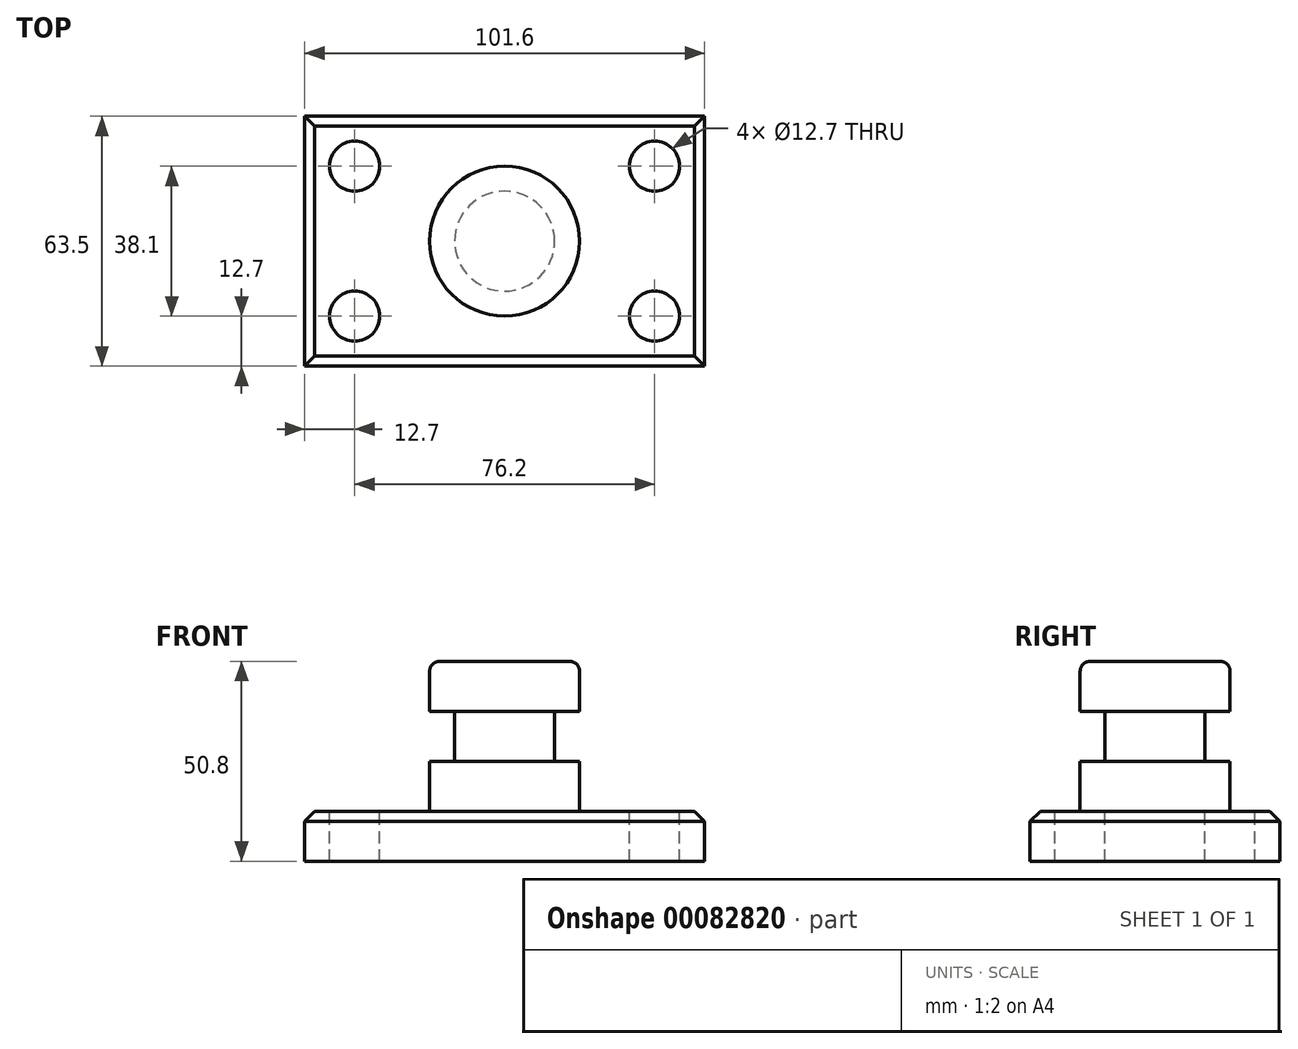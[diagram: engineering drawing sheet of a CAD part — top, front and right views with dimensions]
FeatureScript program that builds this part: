
annotation { "Feature Type Name" : "Feature", "Feature Type Description" : "" }
export const myFeature = defineFeature(function(context is Context, id is Id, definition is map)
    precondition{}
    {
        {
            var Q0;
            Q0=qCreatedBy(makeId("Top.planeOp"),FACE);
            var sketch = newSketch(context, id + "F0", { "sketchPlane" : qUnion([Q0])});
            skLineSegment(sketch, "E0.bottom", {"start": v(-50.8, 31.75) * mm, "end": v(50.8, 31.75) * mm});
            skLineSegment(sketch, "E0.top", {"start": v(-50.8, -31.75) * mm, "end": v(50.8, -31.75) * mm});
            skLineSegment(sketch, "E0.left", {"start": v(-50.8, 31.75) * mm, "end": v(-50.8, -31.75) * mm});
            skLineSegment(sketch, "E0.right", {"start": v(50.8, 31.75) * mm, "end": v(50.8, -31.75) * mm});
            skSolve(sketch);
        }
        {
            var Q0;
            Q0=makeQuery(id+"F0.imprint","IMPRINT",FACE,{"disambiguationData":[TD([[makeQuery(id+"F0.imprint","IMPRINT",EDGE,{"derivedFrom":sQuery(id+"F0.wireOp",EDGE,"E0.bottom")}),-1.0]])]});
            extrude(context, id + "F1", {"entities" : qUnion([Q0]), "depth" : 12.7 * mm});
        }
        {
            var Q0;
            Q0=makeQuery(id+"F1.opExtrude","CAP_FACE",FACE,{"disambiguationData":[OSD([sQuery(id+"F0.wireOp",EDGE,"E0.bottom"),sQuery(id+"F0.wireOp",EDGE,"E0.top"),sQuery(id+"F0.wireOp",EDGE,"E0.left"),sQuery(id+"F0.wireOp",EDGE,"E0.right")])],"isStart":false});
            var sketch = newSketch(context, id + "F2", { "sketchPlane" : qUnion([Q0])});
            skCircle(sketch, "E1", {"center": v(-38.1, 19.05) * mm, "radius": 6.35 * mm});
            skCircle(sketch, "E2", {"center": v(-38.1, -19.05) * mm, "radius": 6.35 * mm});
            skCircle(sketch, "E3.MirrorC", {"center": v(38.1, 19.05) * mm, "radius": 6.35 * mm});
            skCircle(sketch, "E4.MirrorC", {"center": v(38.1, -19.05) * mm, "radius": 6.35 * mm});
            skSolve(sketch);
        }
        {
            var Q0;
            Q0 = qSketchRegion(id + "F2", true);
            extrude(context, id + "F3", {"entities" : qUnion([Q0]), "operationType" : NewBodyOperationType.REMOVE, "endBound" : BoundingType.THROUGH_ALL, "oppositeDirection" : true, "depth" : 25.4 * mm});
        }
        {
            var Q0;
            Q0=qCreatedBy(makeId("Front.planeOp"),FACE);
            var sketch = newSketch(context, id + "F4", { "sketchPlane" : qUnion([Q0])});
            skLineSegment(sketch, "E5", {"start": v(0, 12.7) * mm, "end": v(0, 50.8) * mm});
            skLineSegment(sketch, "E6", {"start": v(0, 50.8) * mm, "end": v(-19.05, 50.8) * mm});
            skLineSegment(sketch, "E7", {"start": v(-19.05, 50.8) * mm, "end": v(-19.05, 12.7) * mm});
            skLineSegment(sketch, "E8", {"start": v(-19.05, 12.7) * mm, "end": v(0, 12.7) * mm});
            skSolve(sketch);
        }
        {
            var Q0;
            Q0 = qSketchRegion(id + "F4", true);
            var Q1;
            Q1=sQuery(id+"F4.wireOp",EDGE,"E5");
            revolve(context, id + "F5", {"operationType" : NewBodyOperationType.ADD, "entities" : qUnion([Q0]), "axis" : qUnion([Q1]), "revolveType" : RevolveType.FULL});
        }
        {
            var Q0;
            Q0=qCreatedBy(makeId("Front.planeOp"),FACE);
            var sketch = newSketch(context, id + "F6", { "sketchPlane" : qUnion([Q0])});
            skLineSegment(sketch, "E9.bottom", {"start": v(19.05, 38.1) * mm, "end": v(12.7, 38.1) * mm});
            skLineSegment(sketch, "E9.top", {"start": v(19.05, 25.4) * mm, "end": v(12.7, 25.4) * mm});
            skLineSegment(sketch, "E9.left", {"start": v(19.05, 38.1) * mm, "end": v(19.05, 25.4) * mm});
            skLineSegment(sketch, "E9.right", {"start": v(12.7, 38.1) * mm, "end": v(12.7, 25.4) * mm});
            skLineSegment(sketch, "E10", {"start": v(19.05, 50.8) * mm, "end": v(19.05, 12.7) * mm});
            skSolve(sketch);
        }
        {
            var Q0;
            Q0 = qSketchRegion(id + "F6", true);
            var Q1;
            Q1=makeQuery(id+"F5.opRevolve","SWEPT_FACE",FACE,{"disambiguationData":[OSD([sQuery(id+"F4.wireOp",EDGE,"E7")])]});
            revolve(context, id + "F7", {"operationType" : NewBodyOperationType.REMOVE, "entities" : qUnion([Q0]), "axis" : qUnion([Q1]), "revolveType" : RevolveType.FULL, "oppositeDirection" : true});
        }
        {
            var Q0;
            Q0=makeQuery(id+"F5.opRevolve","SWEPT_EDGE",EDGE,{"disambiguationData":[OSD([sQuery(id+"F4.wireOp",EDGE,"E6"),sQuery(id+"F4.wireOp",EDGE,"E7")])]});
            var Q1;
            Q1=makeQuery(id+"F5.opRevolve","SWEPT_EDGE",EDGE,{"disambiguationData":[OSD([sQuery(id+"F4.wireOp",EDGE,"E7"),sQuery(id+"F4.wireOp",EDGE,"E8")])]});
            fillet(context, id + "F8", {"entities" : qUnion([Q0, Q1]), "radius" : 2.54 * mm, "tangentPropagation" : true, "allowEdgeOverflow" : false});
        }
        {
            var Q0;
            Q0=makeQuery(id+"F1.opExtrude","CAP_EDGE",EDGE,{"disambiguationData":[OSD([sQuery(id+"F0.wireOp",EDGE,"E0.top")])],"isStart":false});
            var Q1;
            Q1=makeQuery(id+"F1.opExtrude","CAP_EDGE",EDGE,{"disambiguationData":[OSD([sQuery(id+"F0.wireOp",EDGE,"E0.left")])],"isStart":false});
            var Q2;
            Q2=makeQuery(id+"F1.opExtrude","CAP_EDGE",EDGE,{"disambiguationData":[OSD([sQuery(id+"F0.wireOp",EDGE,"E0.bottom")])],"isStart":false});
            var Q3;
            Q3=makeQuery(id+"F1.opExtrude","CAP_EDGE",EDGE,{"disambiguationData":[OSD([sQuery(id+"F0.wireOp",EDGE,"E0.right")])],"isStart":false});
            chamfer(context, id + "F9", {"entities" : qUnion([Q0, Q1, Q2, Q3]), "width" : 2.54 * mm, "tangentPropagation" : true});
        }
    });
